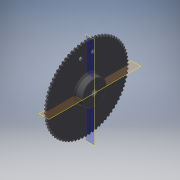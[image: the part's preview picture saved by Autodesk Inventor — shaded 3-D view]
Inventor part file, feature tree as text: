
AUTODESK INVENTOR PART (.ipt)
format: ipt  version: 2018 (Build 220112000, 112)  size: 888,320 bytes
history: native  units: mm
features: sketch x3, revolve x1, extrude x1, hole x1
ambient origin geometry x8: Origin, YZ Plane, XZ Plane, XY Plane, X Axis, Y Axis, Z Axis, Center Point
bodies: Solid1 (feature_tree), body_XY (feature_tree), body_YZ (feature_tree), body_ZX (feature_tree), body_X (feature_tree), body_Y (feature_tree), body_Z (feature_tree), body_Center (feature_tree)
feature tree (6):
  revolve  "Revolution1"  [1 undecoded]
  extrude  "Extrusion1"  Depth=160.412mm
  hole  "穴2"  [1 undecoded]
  sketch  "Sketch_5"  dims[d0=360.0deg d1=4.7mm d2=0.0mm]
  sketch  "Sketch_7"  dims[d3=0.0mm d15=160.412mm d16=164.0mm d17=10.5mm d18=6.0mm d19=4.0mm d20=2.0mm d21=90.0deg d22=8.0mm d23=20.594885mm]
  sketch  "スケッチ8"
note: 2 required parameter values undecoded (feature->parameter linkage not recoverable at this tier; creation-order binding heuristic only, values carry confidence <= 0.55)